# Revit family: Lighting_Fixture-Visa_Lighting-Symmetry_DL
name_source: partatom
category: Lighting Fixtures
units: mm (PartAtom-declared; Revit-internal decimal feet)

## family parameters
Cut with Voids When Loaded = No
Host = Face
Light Source = Yes
OmniClass Number = 23.80.70.11
OmniClass Title = Luminaries for Internal Lighting
Part Type = Normal
Room Calculation Point = No
Round Connector Dimension = Use Diameter
Shared = No

## types (1)
- Not A Type - Load Type Catalog
    Apparent Load = 332 VA
    Assembly Code = D5020200
    Bracket Length = 1' - 6"
    Bracket Width = 1' - 6"
    C 23in Reflector = Yes
    C 45in Reflector = No
    C Constraint = 0
    C Driver Height = 0' - 4 3/4"
    C Driver Length = 0' - 6 125/128"
    C Driver Width = 0' - 6 125/128"
    C Lens Diameter = 0' - 6 125/128"
    Color Filter = 16777215
    Default Elevation = 0' - 0"
    Description = High-abuse downlight with a 4” diameter aperture.
    Desired Bracket Length = 1' - 6"
    Desired Bracket Width = 1' - 6"
    Diameter = 0' - 6 125/128"
    Dimming Lamp Color Temperature Shift = <None>
    Emit Shape Visible in Rendering = No
    Emit from Circle Diameter = 0' - 6 125/128"
    Finish = Paint - VISA - Traffic White (TRWT)
    Frequency = 0 Hz
    Height = 0' - 4 3/4"
    Instruction Sheet Link = https://www.visalighting.com
    Keynote = 26 51 00
    Lamp = LED
    Lens = Acrylic - VISA - Light
    Load Classification = Lighting
    Manufacturer = Visa Lighting
    Model = Please Load Accompanying Type Catalog (.txt)
    Number of Poles = 1
    Phase = 1
    Photometric Web File = CM1885-W-L35K (AMB).ies
    Photometry Note = Please load ies file listed under Photometric Web File for accurate rendering.
    Power Factor = 1
    Product Documentation Link = https://www.visalighting.com
    Product Name = Symmetry DL
    Product Page URL = https://www.visalighting.com
    Recessed Depth = 0' - 2 7/8"
    Recessed Width = 0' - 6 125/128"
    Tilt Angle = 90.00°
    URL = https://www.visalighting.com
    Version = 2020 - V1.0a
    Voltage = 120 V
    Voltage Comment = 120 - 277 Volts Universal
    Warranty URL = https://www.visalighting.com
    Wattage Comments = 50.7 Watts

## geometry (parser evidence)
native form markers: Sweep x2
no freeform markers — native parametric forms only
